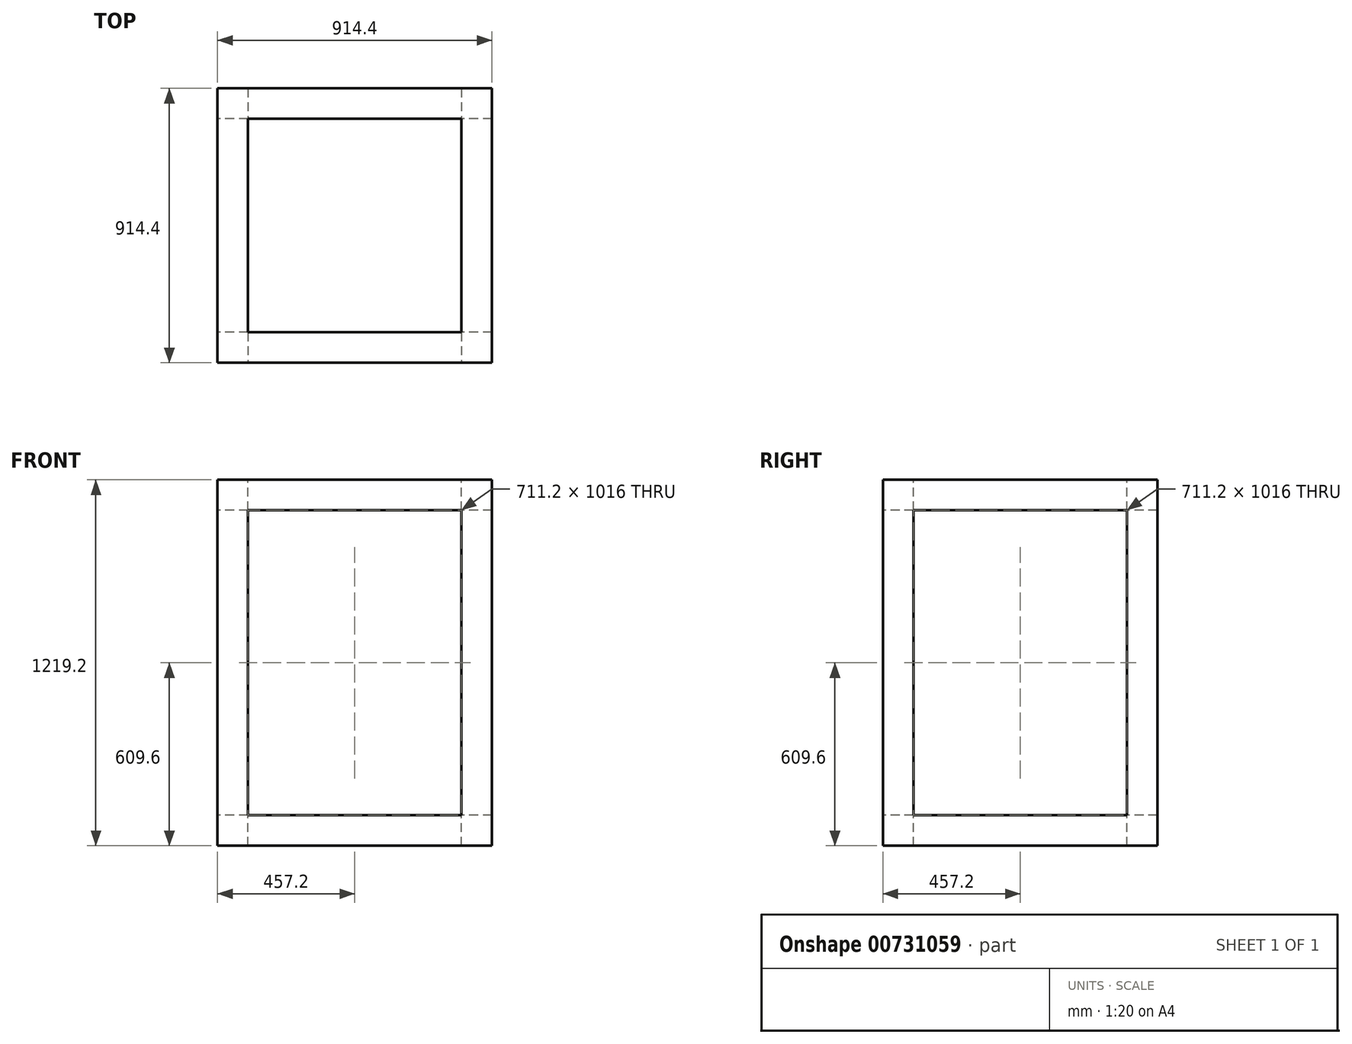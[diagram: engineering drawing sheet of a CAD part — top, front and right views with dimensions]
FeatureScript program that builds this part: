
annotation { "Feature Type Name" : "Feature", "Feature Type Description" : "" }
export const myFeature = defineFeature(function(context is Context, id is Id, definition is map)
    precondition{}
    {
        {
            var Q0;
            Q0=qCreatedBy(makeId("Front.planeOp"),FACE);
            var sketch = newSketch(context, id + "F0", { "sketchPlane" : qUnion([Q0])});
            skLineSegment(sketch, "E0.bottom", {"start": v(457.2, -609.6) * mm, "end": v(-457.2, -609.6) * mm});
            skLineSegment(sketch, "E0.top", {"start": v(457.2, 609.6) * mm, "end": v(-457.2, 609.6) * mm});
            skLineSegment(sketch, "E0.left", {"start": v(457.2, -609.6) * mm, "end": v(457.2, 609.6) * mm});
            skLineSegment(sketch, "E0.right", {"start": v(-457.2, -609.6) * mm, "end": v(-457.2, 609.6) * mm});
            skPoint(sketch, "E0.middle", {"position": v(0, 0) * mm});
            skLineSegment(sketch, "E1.bottom", {"start": v(355.6, -508) * mm, "end": v(-355.6, -508) * mm});
            skLineSegment(sketch, "E1.top", {"start": v(355.6, 508) * mm, "end": v(-355.6, 508) * mm});
            skLineSegment(sketch, "E1.left", {"start": v(355.6, -508) * mm, "end": v(355.6, 508) * mm});
            skLineSegment(sketch, "E1.right", {"start": v(-355.6, -508) * mm, "end": v(-355.6, 508) * mm});
            skSolve(sketch);
        }
        {
            var Q0;
            Q0=makeQuery(id+"F0.imprint","IMPRINT",FACE,{"disambiguationData":[TD([[makeQuery(id+"F0.imprint","IMPRINT",EDGE,{"derivedFrom":sQuery(id+"F0.wireOp",EDGE,"E0.bottom")}),-1.0]])]});
            extrude(context, id + "F1", {"entities" : qUnion([Q0]), "oppositeDirection" : true, "depth" : 914.4 * mm, "offsetDistance" : 25.4 * mm});
        }
        {
            var Q0;
            Q0=makeQuery(id+"F1.opExtrude","SWEPT_FACE",FACE,{"disambiguationData":[OSD([sQuery(id+"F0.wireOp",EDGE,"E0.top")])]});
            var sketch = newSketch(context, id + "F2", { "sketchPlane" : qUnion([Q0])});
            skPoint(sketch, "E2", {"position": v(0, 457.2) * mm});
            skPoint(sketch, "E2.positionSnap0", {"position": v(457.2, 457.2) * mm});
            skLineSegment(sketch, "E3.bottom", {"start": v(355.6, 101.6) * mm, "end": v(-355.6, 101.6) * mm});
            skLineSegment(sketch, "E3.top", {"start": v(355.6, 812.8) * mm, "end": v(-355.6, 812.8) * mm});
            skLineSegment(sketch, "E3.left", {"start": v(355.6, 101.6) * mm, "end": v(355.6, 812.8) * mm});
            skLineSegment(sketch, "E3.right", {"start": v(-355.6, 101.6) * mm, "end": v(-355.6, 812.8) * mm});
            skSolve(sketch);
        }
        {
            var Q0;
            Q0=makeQuery(id+"F2.imprint","IMPRINT",FACE,{"disambiguationData":[TD([[makeQuery(id+"F2.imprint","IMPRINT",EDGE,{"derivedFrom":sQuery(id+"F2.wireOp",EDGE,"E3.bottom")}),-1.0]])]});
            extrude(context, id + "F3", {"entities" : qUnion([Q0]), "operationType" : NewBodyOperationType.REMOVE, "oppositeDirection" : true, "depth" : 1219.2 * mm, "offsetDistance" : 25.4 * mm});
        }
        {
            var Q0;
            Q0=makeQuery(id+"F1.opExtrude","SWEPT_FACE",FACE,{"disambiguationData":[OSD([sQuery(id+"F0.wireOp",EDGE,"E0.right")])]});
            var sketch = newSketch(context, id + "F4", { "sketchPlane" : qUnion([Q0])});
            skLineSegment(sketch, "E4.bottom", {"start": v(-101.6, -508) * mm, "end": v(-812.8, -508) * mm});
            skLineSegment(sketch, "E4.top", {"start": v(-101.6, 508) * mm, "end": v(-812.8, 508) * mm});
            skLineSegment(sketch, "E4.left", {"start": v(-101.6, -508) * mm, "end": v(-101.6, 508) * mm});
            skLineSegment(sketch, "E4.right", {"start": v(-812.8, -508) * mm, "end": v(-812.8, 508) * mm});
            skPoint(sketch, "E4.middle", {"position": v(-457.2, 0) * mm});
            skPoint(sketch, "E4.middle.positionSnap0", {"position": v(-457.2, 609.6) * mm});
            skPoint(sketch, "E4.centerSnap0", {"position": v(-457.2, 609.6) * mm});
            skSolve(sketch);
        }
        {
            var Q0;
            Q0=makeQuery(id+"F4.imprint","IMPRINT",FACE,{"disambiguationData":[TD([[makeQuery(id+"F4.imprint","IMPRINT",EDGE,{"derivedFrom":sQuery(id+"F4.wireOp",EDGE,"E4.bottom")}),-1.0]])]});
            extrude(context, id + "F5", {"entities" : qUnion([Q0]), "operationType" : NewBodyOperationType.REMOVE, "oppositeDirection" : true, "depth" : 914.4 * mm, "offsetDistance" : 25.4 * mm});
        }
    });
